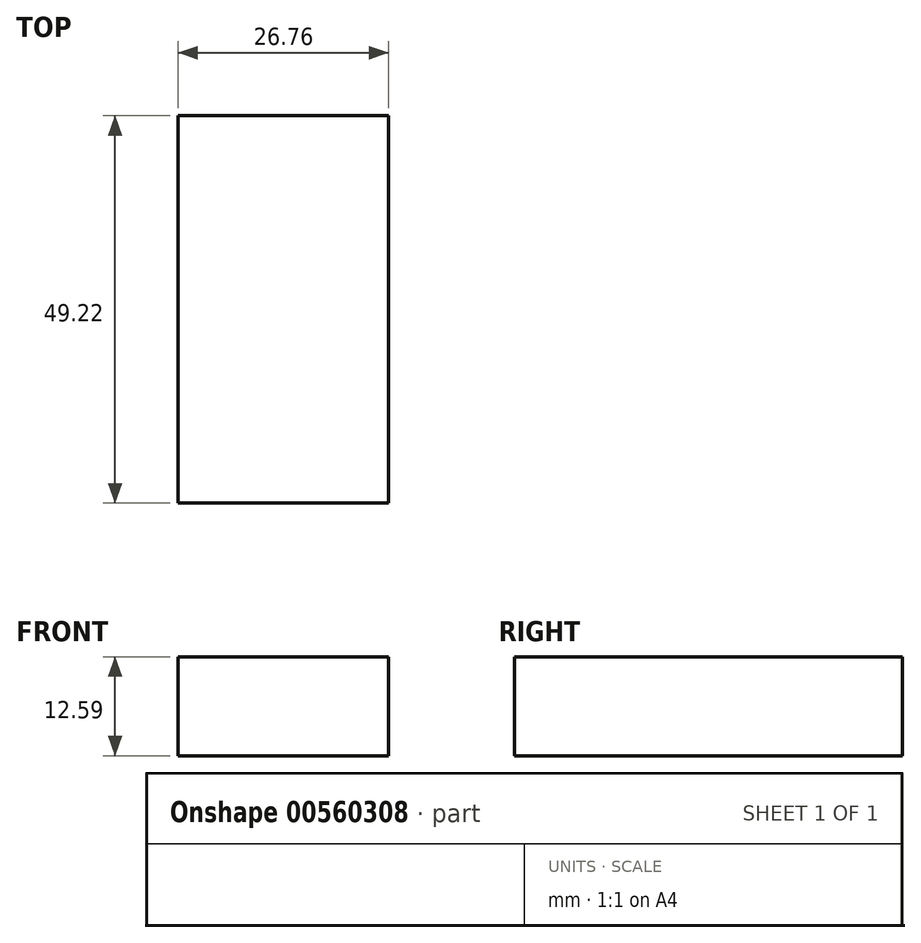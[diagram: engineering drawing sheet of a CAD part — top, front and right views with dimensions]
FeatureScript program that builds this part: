
annotation { "Feature Type Name" : "Feature", "Feature Type Description" : "" }
export const myFeature = defineFeature(function(context is Context, id is Id, definition is map)
    precondition{}
    {
        {
            var Q0;
            Q0=qCreatedBy(makeId("Front.planeOp"),FACE);
            var sketch = newSketch(context, id + "F0", { "sketchPlane" : qUnion([Q0])});
            skLineSegment(sketch, "E0.bottom", {"start": v(-26.76, 49.25) * mm, "end": v(0, 49.25) * mm});
            skLineSegment(sketch, "E0.top", {"start": v(-26.76, 36.66) * mm, "end": v(0, 36.66) * mm});
            skLineSegment(sketch, "E0.left", {"start": v(-26.76, 49.25) * mm, "end": v(-26.76, 36.66) * mm});
            skLineSegment(sketch, "E0.right", {"start": v(0, 49.25) * mm, "end": v(0, 36.66) * mm});
            skSolve(sketch);
        }
        {
            var Q0;
            Q0=makeQuery(id+"F0.imprint","IMPRINT",FACE,{"disambiguationData":[TD([[makeQuery(id+"F0.imprint","IMPRINT",EDGE,{"derivedFrom":sQuery(id+"F0.wireOp",EDGE,"E0.bottom")}),-1.0]])]});
            extrude(context, id + "F1", {"entities" : qUnion([Q0]), "depth" : 49.22 * mm, "offsetDistance" : 25.4 * mm});
        }
    });
